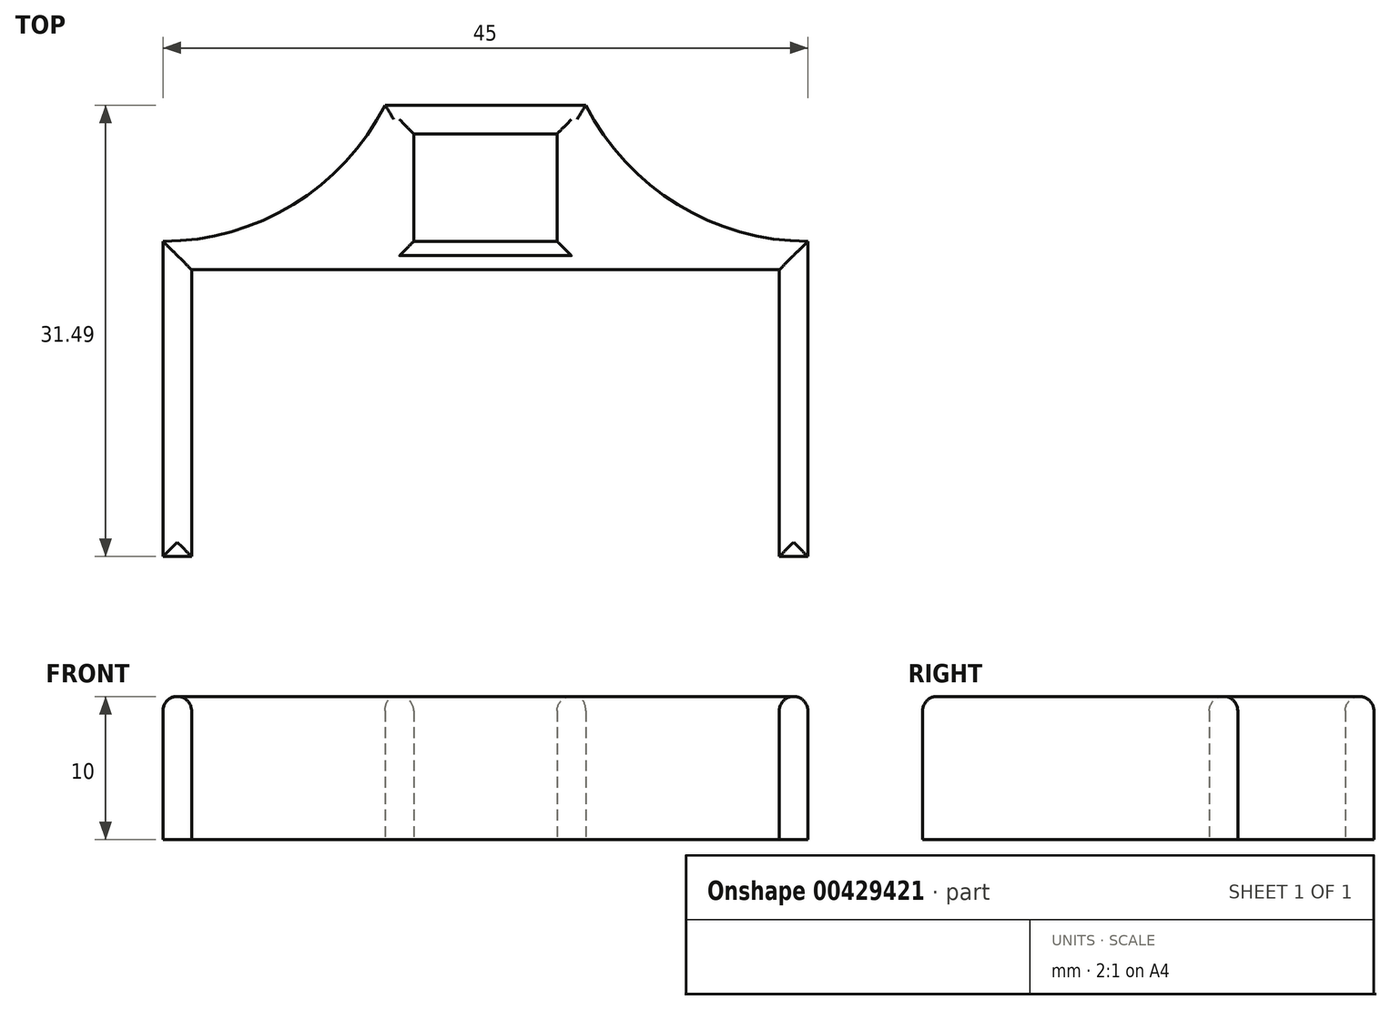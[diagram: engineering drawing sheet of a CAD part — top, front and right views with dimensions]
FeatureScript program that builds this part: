
annotation { "Feature Type Name" : "Feature", "Feature Type Description" : "" }
export const myFeature = defineFeature(function(context is Context, id is Id, definition is map)
    precondition{}
    {
        {
            var Q0;
            Q0=qCreatedBy(makeId("Top.planeOp"),FACE);
            var sketch = newSketch(context, id + "F0", { "sketchPlane" : qUnion([Q0])});
            skLineSegment(sketch, "E0", {"start": v(41, 34.87) * mm, "end": v(41, 14.87) * mm});
            skLineSegment(sketch, "E1", {"start": v(41, 14.87) * mm, "end": v(43, 14.87) * mm});
            skLineSegment(sketch, "E2", {"start": v(43, 14.87) * mm, "end": v(43, 36.86) * mm});
            skLineSegment(sketch, "E3", {"start": v(27.5, 46.36) * mm, "end": v(13.5, 46.36) * mm});
            skLineSegment(sketch, "E4", {"start": v(-2, 36.86) * mm, "end": v(-2, 14.87) * mm});
            skLineSegment(sketch, "E5", {"start": v(-2, 14.87) * mm, "end": v(0, 14.87) * mm});
            skLineSegment(sketch, "E6", {"start": v(0, 14.87) * mm, "end": v(0, 34.87) * mm});
            skLineSegment(sketch, "E7", {"start": v(0, 34.87) * mm, "end": v(41, 34.87) * mm});
            skLineSegment(sketch, "E8", {"start": v(25.5, 36.86) * mm, "end": v(25.5, 44.36) * mm});
            skLineSegment(sketch, "E9", {"start": v(25.5, 44.36) * mm, "end": v(15.5, 44.36) * mm});
            skLineSegment(sketch, "E10", {"start": v(15.5, 44.36) * mm, "end": v(15.5, 36.86) * mm});
            skLineSegment(sketch, "E11", {"start": v(15.5, 36.86) * mm, "end": v(25.5, 36.86) * mm});
            skArc(sketch, "E12", {"start": v(-2, 36.86) * mm, "mid": v(7.09, 39.42) * mm, "end": v(13.5, 46.36) * mm});
            skArc(sketch, "E13", {"start": v(27.5, 46.36) * mm, "mid": v(33.91, 39.42) * mm, "end": v(43, 36.86) * mm});
            skSolve(sketch);
        }
        {
            var Q0;
            Q0 = qSketchRegion(id + "F0", true);
            extrude(context, id + "F1", {"entities" : qUnion([Q0]), "depth" : 10 * mm, "offsetDistance" : 25 * mm});
        }
        {
            var Q0;
            Q0=makeQuery(id+"F1.opExtrude","CAP_FACE",FACE,{"disambiguationData":[OSD([sQuery(id+"F0.wireOp",EDGE,"E0"),sQuery(id+"F0.wireOp",EDGE,"E1"),sQuery(id+"F0.wireOp",EDGE,"E2"),sQuery(id+"F0.wireOp",EDGE,"E3"),sQuery(id+"F0.wireOp",EDGE,"E4"),sQuery(id+"F0.wireOp",EDGE,"E5"),sQuery(id+"F0.wireOp",EDGE,"E6"),sQuery(id+"F0.wireOp",EDGE,"E7"),sQuery(id+"F0.wireOp",EDGE,"E8"),sQuery(id+"F0.wireOp",EDGE,"E9"),sQuery(id+"F0.wireOp",EDGE,"E10"),sQuery(id+"F0.wireOp",EDGE,"E11"),sQuery(id+"F0.wireOp",EDGE,"E12"),sQuery(id+"F0.wireOp",EDGE,"E13")])],"isStart":false});
            fillet(context, id + "F2", {"entities" : qUnion([Q0]), "radius" : 1 * mm, "tangentPropagation" : true, "allowEdgeOverflow" : false});
        }
    });
